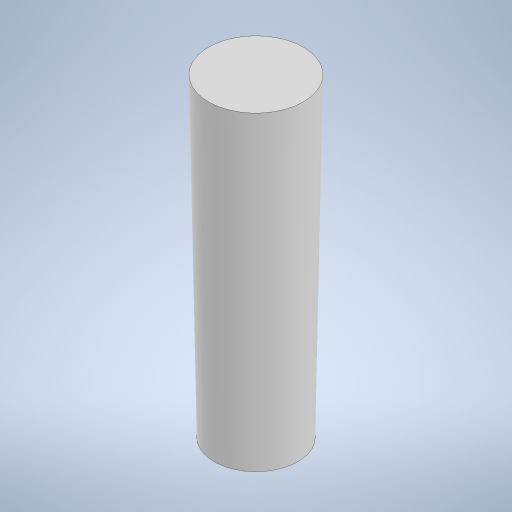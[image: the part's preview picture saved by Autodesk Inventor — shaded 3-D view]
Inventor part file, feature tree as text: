
AUTODESK INVENTOR PART (.ipt)
format: ipt  version: 2023 (Build 270158000, 158)  size: 224,768 bytes
history: native  units: in
note: dims shown in document units (in); Inventor stores cm internally (conversion verified against a paired STEP export)
features: extrude x1, draft x1, sketch x1
ambient origin geometry x8: Origin, YZ Plane, XZ Plane, XY Plane, X Axis, Y Axis, Z Axis, Center Point
bodies: Solid1 (feature_tree)
feature tree (3):
  extrude  "Extrusion1"  Depth=6.0in TaperAngle=0.0deg
  draft  "FaceDraft1"
  sketch  "Sketch1"  dims[d0=1.6in d1=6.0in d2=0.0in d3=-0.0069in]
